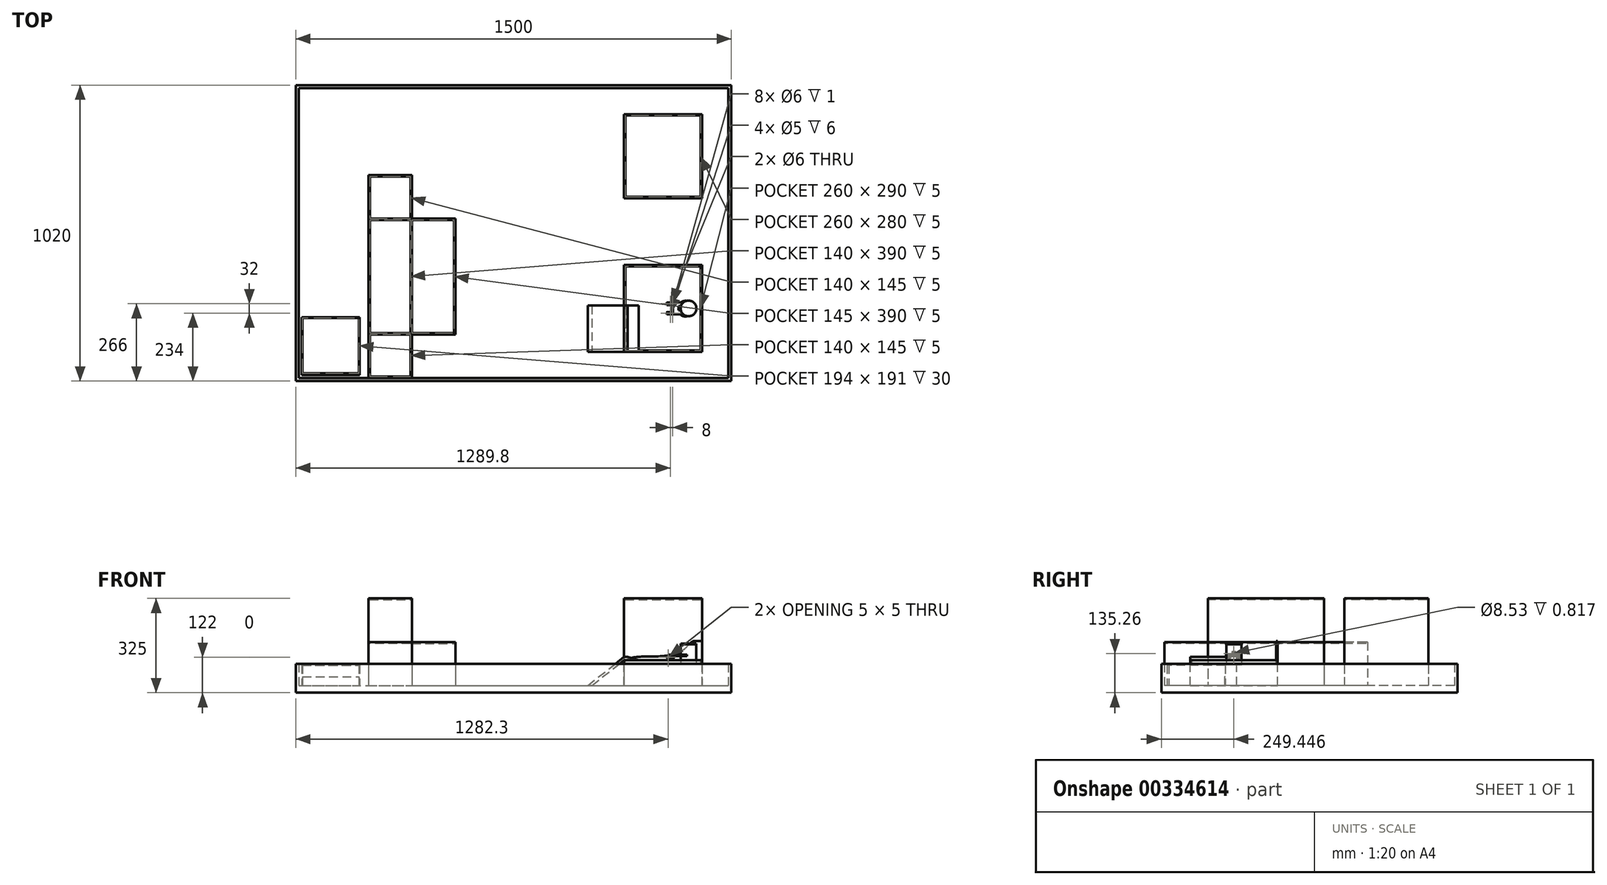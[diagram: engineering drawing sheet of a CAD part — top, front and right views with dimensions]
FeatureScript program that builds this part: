
annotation { "Feature Type Name" : "Feature", "Feature Type Description" : "" }
export const myFeature = defineFeature(function(context is Context, id is Id, definition is map)
    precondition{}
    {
        {
            var Q0;
            Q0=qCreatedBy(makeId("Top.planeOp"),FACE);
            var sketch = newSketch(context, id + "F0", { "sketchPlane" : qUnion([Q0])});
            skCircle(sketch, "E0", {"center": v(0, 0) * mm, "radius": 27.2 * mm});
            skSolve(sketch);
        }
        {
            var Q0;
            Q0=qSketchRegion(id+"F0",true);
            extrude(context, id + "F1", {"entities" : qUnion([Q0]), "depth" : 2.83 * mm});
        }
        {
            var Q0;
            Q0=makeQuery(id+"F1.opExtrude","CAP_FACE",FACE,{"disambiguationData":[OSD([sQuery(id+"F0.wireOp",EDGE,"E0")])],"isStart":false});
            var sketch = newSketch(context, id + "F2", { "sketchPlane" : qUnion([Q0])});
            skCircle(sketch, "E1", {"center": v(0, 0) * mm, "radius": 26.4 * mm});
            skSolve(sketch);
        }
        {
            var Q0;
            Q0=qSketchRegion(id+"F2",true);
            extrude(context, id + "F3", {"entities" : qUnion([Q0]), "operationType" : NewBodyOperationType.ADD, "depth" : 67.36 * mm});
        }
        {
            var Q0;
            Q0=makeQuery(id+"F3.opExtrude","CAP_FACE",FACE,{"disambiguationData":[OSD([sQuery(id+"F2.wireOp",EDGE,"E1")])],"isStart":false});
            var sketch = newSketch(context, id + "F4", { "sketchPlane" : qUnion([Q0])});
            skCircle(sketch, "E2", {"center": v(0, 0) * mm, "radius": 27.2 * mm});
            skSolve(sketch);
        }
        {
            var Q0;
            Q0=qSketchRegion(id+"F4",true);
            extrude(context, id + "F5", {"entities" : qUnion([Q0]), "operationType" : NewBodyOperationType.ADD, "depth" : 2.83 * mm});
        }
        {
            var Q0;
            Q0=makeQuery(id+"F5.opExtrude","CAP_FACE",FACE,{"disambiguationData":[OSD([sQuery(id+"F4.wireOp",EDGE,"E2")])],"isStart":false});
            var sketch = newSketch(context, id + "F6", { "sketchPlane" : qUnion([Q0])});
            skSolve(sketch);
        }
        {
            var Q0;
            Q0=qCreatedBy(makeId("Top.planeOp"),FACE);
            cPlane(context, id + "F7", {"entities" : qUnion([Q0]), "cplaneType" : CPlaneType.OFFSET, "offset" : 25 * mm, "width" : 150 * mm, "height" : 150 * mm});
        }
        {
            var Q0;
            Q0=makeQuery(id+"F6.imprint","IMPRINT",FACE,{"disambiguationData":[TD([[makeQuery(id+"F6.imprint","IMPRINT",EDGE,{"derivedFrom":makeQuery(id+"F5.opExtrude","CAP_EDGE",EDGE,{"disambiguationData":[OSD([sQuery(id+"F4.wireOp",EDGE,"E2")])],"isStart":false})}),1.0]])]});
            var sketch = newSketch(context, id + "F8", { "sketchPlane" : qUnion([Q0])});
            skSolve(sketch);
        }
        {
            var Q0;
            Q0=qCreatedBy(makeId("Top.planeOp"),FACE);
            var sketch = newSketch(context, id + "F9", { "sketchPlane" : qUnion([Q0])});
            skLineSegment(sketch, "E3.bottom", {"start": v(-222.8, -150) * mm, "end": v(47.2, -150) * mm});
            skLineSegment(sketch, "E3.top", {"start": v(-222.8, 150) * mm, "end": v(47.2, 150) * mm});
            skLineSegment(sketch, "E3.left", {"start": v(-222.8, -150) * mm, "end": v(-222.8, 150) * mm});
            skLineSegment(sketch, "E3.right", {"start": v(47.2, -150) * mm, "end": v(47.2, 150) * mm});
            skSolve(sketch);
        }
        {
            var Q0;
            Q0=qSketchRegion(id+"F9",true);
            extrude(context, id + "F10", {"entities" : qUnion([Q0]), "oppositeDirection" : true, "depth" : 72 * mm});
        }
        {
            var Q0;
            Q0=makeQuery(id+"F10.opExtrude","CAP_FACE",FACE,{"disambiguationData":[OSD([sQuery(id+"F9.wireOp",EDGE,"E3.bottom"),sQuery(id+"F9.wireOp",EDGE,"E3.top"),sQuery(id+"F9.wireOp",EDGE,"E3.left"),sQuery(id+"F9.wireOp",EDGE,"E3.right")])],"isStart":true});
            var sketch = newSketch(context, id + "F11", { "sketchPlane" : qUnion([Q0])});
            skLineSegment(sketch, "E4.bottom", {"start": v(-222.8, -150) * mm, "end": v(47.2, -150) * mm});
            skLineSegment(sketch, "E4.top", {"start": v(-222.8, -145) * mm, "end": v(42.2, -145) * mm});
            skLineSegment(sketch, "E4.left", {"start": v(-222.8, -150) * mm, "end": v(-222.8, -145) * mm});
            skLineSegment(sketch, "E5.bottom", {"start": v(47.2, 150) * mm, "end": v(42.2, 150) * mm});
            skLineSegment(sketch, "E5.left", {"start": v(47.2, 150) * mm, "end": v(47.2, -150) * mm});
            skLineSegment(sketch, "E5.right", {"start": v(42.2, 150) * mm, "end": v(42.2, -145) * mm});
            skSolve(sketch);
        }
        {
            var Q0;
            Q0=qSketchRegion(id+"F11",true);
            extrude(context, id + "F12", {"entities" : qUnion([Q0]), "operationType" : NewBodyOperationType.ADD, "depth" : 15 * mm});
        }
        {
            var Q0;
            Q0=makeQuery(id+"F12.boolean.opBoolean","MERGE",FACE,{"derivedFrom":[makeQuery(id+"F10.opExtrude","SWEPT_FACE",FACE,{"disambiguationData":[OSD([sQuery(id+"F9.wireOp",EDGE,"E3.top")])]}),makeQuery(id+"F12.opExtrude","SWEPT_FACE",FACE,{"disambiguationData":[OSD([sQuery(id+"F11.wireOp",EDGE,"E5.bottom")])]})]});
            var sketch = newSketch(context, id + "F13", { "sketchPlane" : qUnion([Q0])});
            skLineSegment(sketch, "E6", {"start": v(-47.2, 81.36) * mm, "end": v(-21.31, 81.36) * mm});
            skFitSpline(sketch, "E7", {"points": [v(-21.31, 81.36) * mm, v(15.24, 52.01) * mm, v(114.14, 28.17) * mm, v(222.8, 0) * mm], "startDerivative": vector(181.02, 0.3) * mm, "endDerivative": vector(-1.73, -239.85) * mm});
            skLineSegment(sketch, "E8", {"start": v(-47.2, 81.36) * mm, "end": v(-47.2, -72) * mm});
            skLineSegment(sketch, "E9", {"start": v(-47.2, -72) * mm, "end": v(222.8, -72) * mm});
            skLineSegment(sketch, "E10", {"start": v(222.8, -72) * mm, "end": v(222.8, 0) * mm});
            skSolve(sketch);
        }
        {
            var Q0;
            Q0=qSketchRegion(id+"F13",true);
            extrude(context, id + "F14", {"entities" : qUnion([Q0]), "operationType" : NewBodyOperationType.ADD, "oppositeDirection" : true, "depth" : 5 * mm});
        }
        {
            var Q0;
            Q0=makeQuery(id+"F10.opExtrude","CAP_FACE",FACE,{"disambiguationData":[OSD([sQuery(id+"F9.wireOp",EDGE,"E3.bottom"),sQuery(id+"F9.wireOp",EDGE,"E3.top"),sQuery(id+"F9.wireOp",EDGE,"E3.left"),sQuery(id+"F9.wireOp",EDGE,"E3.right")])],"isStart":true});
            var sketch = newSketch(context, id + "F15", { "sketchPlane" : qUnion([Q0])});
            skLineSegment(sketch, "E11.bottom", {"start": v(-222.8, 145) * mm, "end": v(-217.8, 145) * mm});
            skLineSegment(sketch, "E11.top", {"start": v(-222.8, -145) * mm, "end": v(-217.8, -145) * mm});
            skLineSegment(sketch, "E11.left", {"start": v(-222.8, 145) * mm, "end": v(-222.8, -145) * mm});
            skLineSegment(sketch, "E11.right", {"start": v(-217.8, 145) * mm, "end": v(-217.8, -145) * mm});
            skSolve(sketch);
        }
        {
            var Q0;
            Q0=qSketchRegion(id+"F15",true);
            extrude(context, id + "F16", {"entities" : qUnion([Q0]), "operationType" : NewBodyOperationType.ADD, "depth" : 5 * mm});
        }
        {
            var Q0;
            Q0=makeQuery(id+"F10.opExtrude","CAP_FACE",FACE,{"disambiguationData":[OSD([sQuery(id+"F9.wireOp",EDGE,"E3.bottom"),sQuery(id+"F9.wireOp",EDGE,"E3.top"),sQuery(id+"F9.wireOp",EDGE,"E3.left"),sQuery(id+"F9.wireOp",EDGE,"E3.right")])],"isStart":false});
            var sketch = newSketch(context, id + "F17", { "sketchPlane" : qUnion([Q0])});
            skLineSegment(sketch, "E12.bottom", {"start": v(147.2, 250) * mm, "end": v(-1352.8, 250) * mm});
            skLineSegment(sketch, "E12.top", {"start": v(147.2, -770) * mm, "end": v(-1352.8, -770) * mm});
            skLineSegment(sketch, "E12.left", {"start": v(147.2, 250) * mm, "end": v(147.2, -770) * mm});
            skLineSegment(sketch, "E12.right", {"start": v(-1352.8, 250) * mm, "end": v(-1352.8, -770) * mm});
            skSolve(sketch);
        }
        {
            var Q0;
            Q0=qSketchRegion(id+"F17",true);
            extrude(context, id + "F18", {"entities" : qUnion([Q0]), "operationType" : NewBodyOperationType.ADD, "depth" : 25 * mm});
        }
        {
            var Q0;
            Q0=makeQuery(id+"F18.opExtrude","CAP_FACE",FACE,{"disambiguationData":[OSD([sQuery(id+"F17.wireOp",EDGE,"E12.bottom"),sQuery(id+"F17.wireOp",EDGE,"E12.top"),sQuery(id+"F17.wireOp",EDGE,"E12.left"),sQuery(id+"F17.wireOp",EDGE,"E12.right")])],"isStart":true});
            var sketch = newSketch(context, id + "F19", { "sketchPlane" : qUnion([Q0])});
            skLineSegment(sketch, "E13.bottom", {"start": v(-222.8, 670) * mm, "end": v(47.2, 670) * mm});
            skLineSegment(sketch, "E13.top", {"start": v(-222.8, 380) * mm, "end": v(47.2, 380) * mm});
            skLineSegment(sketch, "E13.left", {"start": v(-222.8, 670) * mm, "end": v(-222.8, 380) * mm});
            skLineSegment(sketch, "E13.right", {"start": v(47.2, 670) * mm, "end": v(47.2, 380) * mm});
            skSolve(sketch);
        }
        {
            var Q0;
            Q0=qSketchRegion(id+"F19",true);
            extrude(context, id + "F20", {"entities" : qUnion([Q0]), "operationType" : NewBodyOperationType.ADD, "depth" : 300 * mm});
        }
        {
            var Q0;
            Q0=makeQuery(id+"F20.opExtrude","CAP_FACE",FACE,{"disambiguationData":[OSD([sQuery(id+"F19.wireOp",EDGE,"E13.bottom"),sQuery(id+"F19.wireOp",EDGE,"E13.top"),sQuery(id+"F19.wireOp",EDGE,"E13.left"),sQuery(id+"F19.wireOp",EDGE,"E13.right")])],"isStart":false});
            var sketch = newSketch(context, id + "F21", { "sketchPlane" : qUnion([Q0])});
            skLineSegment(sketch, "E14.bottom", {"start": v(-217.8, 665) * mm, "end": v(42.2, 665) * mm});
            skLineSegment(sketch, "E14.top", {"start": v(-217.8, 385) * mm, "end": v(42.2, 385) * mm});
            skLineSegment(sketch, "E14.left", {"start": v(-217.8, 665) * mm, "end": v(-217.8, 385) * mm});
            skLineSegment(sketch, "E14.right", {"start": v(42.2, 665) * mm, "end": v(42.2, 385) * mm});
            skSolve(sketch);
        }
        {
            var Q0;
            Q0=qSketchRegion(id+"F21",true);
            extrude(context, id + "F22", {"entities" : qUnion([Q0]), "operationType" : NewBodyOperationType.REMOVE, "oppositeDirection" : true, "depth" : 5 * mm});
        }
        {
            var Q0;
            Q0=makeQuery(id+"F18.opExtrude","CAP_FACE",FACE,{"disambiguationData":[OSD([sQuery(id+"F17.wireOp",EDGE,"E12.bottom"),sQuery(id+"F17.wireOp",EDGE,"E12.top"),sQuery(id+"F17.wireOp",EDGE,"E12.left"),sQuery(id+"F17.wireOp",EDGE,"E12.right")])],"isStart":true});
            var sketch = newSketch(context, id + "F23", { "sketchPlane" : qUnion([Q0])});
            skLineSegment(sketch, "E15.bottom", {"start": v(-1352.8, 770) * mm, "end": v(147.2, 770) * mm});
            skLineSegment(sketch, "E15.top", {"start": v(-1352.8, -250) * mm, "end": v(147.2, -250) * mm});
            skLineSegment(sketch, "E15.left", {"start": v(-1352.8, 770) * mm, "end": v(-1352.8, -250) * mm});
            skLineSegment(sketch, "E15.right", {"start": v(147.2, 770) * mm, "end": v(147.2, -250) * mm});
            skLineSegment(sketch, "E16.bottom", {"start": v(-1342.8, 760) * mm, "end": v(137.2, 760) * mm});
            skLineSegment(sketch, "E16.top", {"start": v(-1342.8, -240) * mm, "end": v(137.2, -240) * mm});
            skLineSegment(sketch, "E16.left", {"start": v(-1342.8, 760) * mm, "end": v(-1342.8, -240) * mm});
            skLineSegment(sketch, "E16.right", {"start": v(137.2, 760) * mm, "end": v(137.2, -240) * mm});
            skSolve(sketch);
        }
        {
            var Q0;
            Q0=qSketchRegion(id+"F23",true);
            extrude(context, id + "F24", {"entities" : qUnion([Q0]), "operationType" : NewBodyOperationType.ADD, "depth" : 75 * mm});
        }
        {
            var Q0;
            Q0=makeQuery(id+"F18.opExtrude","CAP_FACE",FACE,{"disambiguationData":[OSD([sQuery(id+"F17.wireOp",EDGE,"E12.bottom"),sQuery(id+"F17.wireOp",EDGE,"E12.top"),sQuery(id+"F17.wireOp",EDGE,"E12.left"),sQuery(id+"F17.wireOp",EDGE,"E12.right")])],"isStart":true});
            var sketch = newSketch(context, id + "F25", { "sketchPlane" : qUnion([Q0])});
            skLineSegment(sketch, "E17.bottom", {"start": v(-1102.8, 460) * mm, "end": v(-952.8, 460) * mm});
            skLineSegment(sketch, "E17.top", {"start": v(-1102.8, -240) * mm, "end": v(-952.8, -240) * mm});
            skLineSegment(sketch, "E17.left", {"start": v(-1102.8, 460) * mm, "end": v(-1102.8, -240) * mm});
            skLineSegment(sketch, "E17.right", {"start": v(-952.8, 460) * mm, "end": v(-952.8, 310) * mm});
            skLineSegment(sketch, "E18.bottom", {"start": v(-952.8, 310) * mm, "end": v(-802.8, 310) * mm});
            skLineSegment(sketch, "E18.top", {"start": v(-952.8, -90) * mm, "end": v(-802.8, -90) * mm});
            skLineSegment(sketch, "E18.right", {"start": v(-802.8, 310) * mm, "end": v(-802.8, -90) * mm});
            skLineSegment(sketch, "E19.trimOffspring", {"start": v(-952.8, -90) * mm, "end": v(-952.8, -240) * mm});
            skSolve(sketch);
        }
        {
            var Q0;
            Q0=qSketchRegion(id+"F25",true);
            extrude(context, id + "F26", {"entities" : qUnion([Q0]), "operationType" : NewBodyOperationType.ADD, "depth" : 150 * mm});
        }
        {
            var Q0;
            Q0=makeQuery(id+"F26.opExtrude","CAP_FACE",FACE,{"disambiguationData":[OSD([sQuery(id+"F25.wireOp",EDGE,"E17.bottom"),sQuery(id+"F25.wireOp",EDGE,"E17.top"),sQuery(id+"F25.wireOp",EDGE,"E17.left"),sQuery(id+"F25.wireOp",EDGE,"E17.right"),sQuery(id+"F25.wireOp",EDGE,"E18.bottom"),sQuery(id+"F25.wireOp",EDGE,"E18.top"),sQuery(id+"F25.wireOp",EDGE,"E18.right"),sQuery(id+"F25.wireOp",EDGE,"E19.trimOffspring")])],"isStart":false});
            var sketch = newSketch(context, id + "F27", { "sketchPlane" : qUnion([Q0])});
            skLineSegment(sketch, "E20.bottom", {"start": v(-952.8, 310) * mm, "end": v(-1102.8, 310) * mm});
            skLineSegment(sketch, "E20.top", {"start": v(-952.8, -90) * mm, "end": v(-1102.8, -90) * mm});
            skLineSegment(sketch, "E20.left", {"start": v(-952.8, 310) * mm, "end": v(-952.8, -90) * mm});
            skLineSegment(sketch, "E20.right", {"start": v(-1102.8, 310) * mm, "end": v(-1102.8, -90) * mm});
            skSolve(sketch);
        }
        {
            var Q0;
            Q0=qSketchRegion(id+"F27",true);
            extrude(context, id + "F28", {"entities" : qUnion([Q0]), "operationType" : NewBodyOperationType.ADD, "depth" : 150 * mm});
        }
        {
            var Q0;
            Q0=makeQuery(id+"F28.opExtrude","CAP_FACE",FACE,{"disambiguationData":[OSD([sQuery(id+"F27.wireOp",EDGE,"E20.bottom"),sQuery(id+"F27.wireOp",EDGE,"E20.top"),sQuery(id+"F27.wireOp",EDGE,"E20.left"),sQuery(id+"F27.wireOp",EDGE,"E20.right")])],"isStart":false});
            var sketch = newSketch(context, id + "F29", { "sketchPlane" : qUnion([Q0])});
            skLineSegment(sketch, "E21.bottom", {"start": v(-1097.8, 305) * mm, "end": v(-957.8, 305) * mm});
            skLineSegment(sketch, "E21.top", {"start": v(-1097.8, -85) * mm, "end": v(-957.8, -85) * mm});
            skLineSegment(sketch, "E21.left", {"start": v(-1097.8, 305) * mm, "end": v(-1097.8, -85) * mm});
            skLineSegment(sketch, "E21.right", {"start": v(-957.8, 305) * mm, "end": v(-957.8, -85) * mm});
            skSolve(sketch);
        }
        {
            var Q0;
            Q0=qSketchRegion(id+"F29",true);
            extrude(context, id + "F30", {"entities" : qUnion([Q0]), "operationType" : NewBodyOperationType.REMOVE, "oppositeDirection" : true, "depth" : 5 * mm});
        }
        {
            var Q0;
            {var subQ0=sQuery(id+"F25.wireOp",EDGE,"E17.left");var subQ1=sQuery(id+"F25.wireOp",EDGE,"E18.bottom");var subQ2=sQuery(id+"F25.wireOp",EDGE,"E17.right");var subQ3=sQuery(id+"F25.wireOp",EDGE,"E17.bottom");var subQ4=makeQuery(id+"F26.opExtrude","CAP_FACE",FACE,{"disambiguationData":[OSD([subQ3,sQuery(id+"F25.wireOp",EDGE,"E17.top"),subQ0,subQ2,subQ1,sQuery(id+"F25.wireOp",EDGE,"E18.top"),sQuery(id+"F25.wireOp",EDGE,"E18.right"),sQuery(id+"F25.wireOp",EDGE,"E19.trimOffspring")])],"isStart":false});Q0=makeQuery(id+"F28.boolean.opBoolean","SPLIT",FACE,{"disambiguationData":[TD([makeQuery(id+"F26.opExtrude","SWEPT_FACE",FACE,{"disambiguationData":[OSD([subQ3])]})])],"derivedFrom":subQ4});}
            var sketch = newSketch(context, id + "F31", { "sketchPlane" : qUnion([Q0])});
            skLineSegment(sketch, "E22.bottom", {"start": v(-1097.8, 455) * mm, "end": v(-957.8, 455) * mm});
            skLineSegment(sketch, "E22.top", {"start": v(-1097.8, 310) * mm, "end": v(-957.8, 310) * mm});
            skLineSegment(sketch, "E22.left", {"start": v(-1097.8, 455) * mm, "end": v(-1097.8, 310) * mm});
            skLineSegment(sketch, "E22.right", {"start": v(-957.8, 455) * mm, "end": v(-957.8, 310) * mm});
            skLineSegment(sketch, "E23.bottom", {"start": v(-952.8, 305) * mm, "end": v(-807.8, 305) * mm});
            skLineSegment(sketch, "E23.top", {"start": v(-952.8, -85) * mm, "end": v(-807.8, -85) * mm});
            skLineSegment(sketch, "E23.left", {"start": v(-952.8, 305) * mm, "end": v(-952.8, -85) * mm});
            skLineSegment(sketch, "E23.right", {"start": v(-807.8, 305) * mm, "end": v(-807.8, -85) * mm});
            skLineSegment(sketch, "E24.bottom", {"start": v(-1097.8, -90) * mm, "end": v(-957.8, -90) * mm});
            skLineSegment(sketch, "E24.top", {"start": v(-1097.8, -235) * mm, "end": v(-957.8, -235) * mm});
            skLineSegment(sketch, "E24.left", {"start": v(-1097.8, -90) * mm, "end": v(-1097.8, -235) * mm});
            skLineSegment(sketch, "E24.right", {"start": v(-957.8, -90) * mm, "end": v(-957.8, -235) * mm});
            skSolve(sketch);
        }
        {
            var Q0;
            Q0=qSketchRegion(id+"F31",true);
            extrude(context, id + "F32", {"entities" : qUnion([Q0]), "operationType" : NewBodyOperationType.REMOVE, "oppositeDirection" : true, "depth" : 5 * mm});
        }
        {
            var Q0;
            Q0=qCreatedBy(id+"F7.planeOp",FACE);
            var sketch = newSketch(context, id + "F33", { "sketchPlane" : qUnion([Q0])});
            skLineSegment(sketch, "E25", {"start": v(0, 0) * mm, "end": v(-90, 0) * mm, "construction": true});
            skLineSegment(sketch, "E26.bottom", {"start": v(-74.5, -12) * mm, "end": v(-55, -12) * mm});
            skLineSegment(sketch, "E26.top", {"start": v(-74.5, -20) * mm, "end": v(-55, -20) * mm});
            skLineSegment(sketch, "E26.left", {"start": v(-74.5, -12) * mm, "end": v(-74.5, -13) * mm});
            skPoint(sketch, "E27.visualSharp", {"position": v(-51, -12) * mm});
            skPoint(sketch, "E28.visualSharp", {"position": v(-51, -20) * mm});
            skCircle(sketch, "E29", {"center": v(-55, -16) * mm, "radius": 3 * mm});
            skLineSegment(sketch, "E30", {"start": v(-59, -3.98) * mm, "end": v(-59, -18.08) * mm, "construction": true});
            skCircle(sketch, "E31.MirrorC", {"center": v(-63, -16) * mm, "radius": 3 * mm});
            skLineSegment(sketch, "E32.bottom", {"start": v(-74.5, -13) * mm, "end": v(-65.65, -13) * mm});
            skLineSegment(sketch, "E32.top", {"start": v(-74.5, -19) * mm, "end": v(-65.65, -19) * mm});
            skArc(sketch, "E33", {"start": v(-65.65, -13) * mm, "mid": v(-67, -16) * mm, "end": v(-65.65, -19) * mm});
            skLineSegment(sketch, "E34.trimOffspring", {"start": v(-74.5, -19) * mm, "end": v(-74.5, -20) * mm});
            skArc(sketch, "E35.trimOffspring", {"start": v(-55, -20) * mm, "mid": v(-51, -16) * mm, "end": v(-55, -12) * mm});
            skLineSegment(sketch, "E36.MirrorCS", {"start": v(-74.5, 12) * mm, "end": v(-74.5, 13) * mm});
            skLineSegment(sketch, "E37.MirrorCS", {"start": v(-74.5, 19) * mm, "end": v(-74.5, 20) * mm});
            skPoint(sketch, "E38.MirrorP", {"position": v(-51, 12) * mm});
            skLineSegment(sketch, "E39.MirrorCS", {"start": v(-74.5, 12) * mm, "end": v(-55, 12) * mm});
            skPoint(sketch, "E40.MirrorP", {"position": v(-51, 20) * mm});
            skArc(sketch, "E41.MirrorCS", {"start": v(-65.65, 13) * mm, "mid": v(-67, 16) * mm, "end": v(-65.65, 19) * mm});
            skArc(sketch, "E42.MirrorCS", {"start": v(-55, 20) * mm, "mid": v(-51, 16) * mm, "end": v(-55, 12) * mm});
            skLineSegment(sketch, "E43.MirrorCS", {"start": v(-74.5, 20) * mm, "end": v(-55, 20) * mm});
            skCircle(sketch, "E44.MirrorC", {"center": v(-55, 16) * mm, "radius": 3 * mm});
            skCircle(sketch, "E45.MirrorC", {"center": v(-63, 16) * mm, "radius": 3 * mm});
            skLineSegment(sketch, "E46.MirrorCS", {"start": v(-74.5, 19) * mm, "end": v(-65.65, 19) * mm});
            skLineSegment(sketch, "E47.MirrorCS", {"start": v(-74.5, 13) * mm, "end": v(-65.65, 13) * mm});
            skSolve(sketch);
        }
        {
            var Q0;
            Q0=qSketchRegion(id+"F33",true);
            var Q1;
            Q1=qSketchRegion(id+"F36",true);
            extrude(context, id + "F34", {"entities" : qUnion([Q0, Q1]), "endBound" : BoundingType.SYMMETRIC, "depth" : 8 * mm});
        }
        {
            var Q0;
            Q0=makeQuery(id+"F34.opExtrude","CAP_EDGE",EDGE,{"disambiguationData":[OSD([sQuery(id+"F33.wireOp",EDGE,"E34.trimOffspring")])],"isStart":false});
            var Q1;
            Q1=makeQuery(id+"F34.opExtrude","CAP_EDGE",EDGE,{"disambiguationData":[OSD([sQuery(id+"F33.wireOp",EDGE,"E26.left")])],"isStart":false});
            var Q2;
            Q2=makeQuery(id+"F34.opExtrude","CAP_EDGE",EDGE,{"disambiguationData":[OSD([sQuery(id+"F33.wireOp",EDGE,"E34.trimOffspring")])],"isStart":true});
            var Q3;
            Q3=makeQuery(id+"F34.opExtrude","CAP_EDGE",EDGE,{"disambiguationData":[OSD([sQuery(id+"F33.wireOp",EDGE,"E26.left")])],"isStart":true});
            var Q4;
            Q4=makeQuery(id+"F34.opExtrude","CAP_EDGE",EDGE,{"disambiguationData":[OSD([sQuery(id+"F33.wireOp",EDGE,"E36.MirrorCS")])],"isStart":false});
            var Q5;
            Q5=makeQuery(id+"F34.opExtrude","CAP_EDGE",EDGE,{"disambiguationData":[OSD([sQuery(id+"F33.wireOp",EDGE,"E37.MirrorCS")])],"isStart":false});
            var Q6;
            Q6=makeQuery(id+"F34.opExtrude","CAP_EDGE",EDGE,{"disambiguationData":[OSD([sQuery(id+"F33.wireOp",EDGE,"E37.MirrorCS")])],"isStart":true});
            var Q7;
            Q7=makeQuery(id+"F34.opExtrude","CAP_EDGE",EDGE,{"disambiguationData":[OSD([sQuery(id+"F33.wireOp",EDGE,"E36.MirrorCS")])],"isStart":true});
            fillet(context, id + "F35", {"entities" : qUnion([Q0, Q1, Q2, Q3, Q4, Q5, Q6, Q7]), "radius" : 4 * mm, "tangentPropagation" : true, "allowEdgeOverflow" : false});
        }
        {
            var Q0;
            Q0=makeQuery(id+"F34.opExtrude","SWEPT_FACE",FACE,{"disambiguationData":[OSD([sQuery(id+"F33.wireOp",EDGE,"E26.top")])]});
            var sketch = newSketch(context, id + "F36", { "sketchPlane" : qUnion([Q0])});
            skCircle(sketch, "E48", {"center": v(-70.5, 25) * mm, "radius": 3 * mm});
            skSolve(sketch);
        }
        {
            var Q0;
            Q0=qSketchRegion(id+"F36",true);
            var Q1;
            Q1=makeQuery(id+"F34.opExtrude","SWEPT_FACE",FACE,{"disambiguationData":[OSD([sQuery(id+"F33.wireOp",EDGE,"E26.bottom")])]});
            extrude(context, id + "F37", {"entities" : qUnion([Q0]), "operationType" : NewBodyOperationType.ADD, "endBound" : BoundingType.UP_TO_SURFACE, "oppositeDirection" : true, "endBoundEntityFace" : qUnion([Q1]), "depth" : 25 * mm});
        }
        {
            var Q0;
            Q0=makeQuery(id+"F34.opExtrude","SWEPT_FACE",FACE,{"disambiguationData":[OSD([sQuery(id+"F33.wireOp",EDGE,"E43.MirrorCS")])]});
            var sketch = newSketch(context, id + "F38", { "sketchPlane" : qUnion([Q0])});
            skCircle(sketch, "E49", {"center": v(70.5, 25) * mm, "radius": 3 * mm});
            skSolve(sketch);
        }
        {
            var Q0;
            Q0=qSketchRegion(id+"F38",true);
            var Q1;
            Q1=makeQuery(id+"F34.opExtrude","SWEPT_FACE",FACE,{"disambiguationData":[OSD([sQuery(id+"F33.wireOp",EDGE,"E39.MirrorCS")])]});
            extrude(context, id + "F39", {"entities" : qUnion([Q0]), "operationType" : NewBodyOperationType.ADD, "endBound" : BoundingType.UP_TO_SURFACE, "oppositeDirection" : true, "endBoundEntityFace" : qUnion([Q1]), "depth" : 25 * mm});
        }
        {
            var Q0;
            Q0=qCreatedBy(id+"F7.planeOp",FACE);
            var sketch = newSketch(context, id + "F40", { "sketchPlane" : qUnion([Q0])});
            skCircle(sketch, "E50", {"center": v(-55, 16) * mm, "radius": 3 * mm});
            skCircle(sketch, "E51", {"center": v(-63, 16) * mm, "radius": 2.5 * mm});
            skCircle(sketch, "E52", {"center": v(-63, 16) * mm, "radius": 3 * mm});
            skCircle(sketch, "E53", {"center": v(-55, 16) * mm, "radius": 2.5 * mm});
            skSolve(sketch);
        }
        {
            var Q0;
            Q0=qSketchRegion(id+"F40",true);
            extrude(context, id + "F41", {"entities" : qUnion([Q0]), "operationType" : NewBodyOperationType.ADD, "endBound" : BoundingType.SYMMETRIC, "depth" : 6 * mm});
        }
        {
            var Q0;
            Q0=qCreatedBy(id+"F7.planeOp",FACE);
            var sketch = newSketch(context, id + "F42", { "sketchPlane" : qUnion([Q0])});
            skCircle(sketch, "E54", {"center": v(-63, -16) * mm, "radius": 2.5 * mm});
            skCircle(sketch, "E55", {"center": v(-63, -16) * mm, "radius": 3 * mm});
            skCircle(sketch, "E56", {"center": v(-55, -16) * mm, "radius": 2.5 * mm});
            skCircle(sketch, "E57", {"center": v(-55, -16) * mm, "radius": 3 * mm});
            skSolve(sketch);
        }
        {
            var Q0;
            Q0=qSketchRegion(id+"F42",true);
            extrude(context, id + "F43", {"entities" : qUnion([Q0]), "operationType" : NewBodyOperationType.ADD, "endBound" : BoundingType.SYMMETRIC, "depth" : 6 * mm});
        }
        {
            var Q0;
            Q0=makeQuery(id+"F34.opExtrude","SWEPT_FACE",FACE,{"disambiguationData":[OSD([sQuery(id+"F33.wireOp",EDGE,"E43.MirrorCS")])]});
            var sketch = newSketch(context, id + "F44", { "sketchPlane" : qUnion([Q0])});
            skArc(sketch, "E58", {"start": v(71.5, 27.3) * mm, "mid": v(70.5, 27.5) * mm, "end": v(69.5, 27.3) * mm});
            skLineSegment(sketch, "E59.bottom", {"start": v(68.2, 26) * mm, "end": v(69.5, 26) * mm});
            skLineSegment(sketch, "E59.top", {"start": v(68.2, 24) * mm, "end": v(69.5, 24) * mm});
            skLineSegment(sketch, "E60.left", {"start": v(71.5, 27.3) * mm, "end": v(71.5, 26) * mm});
            skLineSegment(sketch, "E60.right", {"start": v(69.5, 27.3) * mm, "end": v(69.5, 26) * mm});
            skPoint(sketch, "E61.orphan", {"position": v(69.5, 27.8) * mm});
            skPoint(sketch, "E62.orphan", {"position": v(71.5, 27.8) * mm});
            skArc(sketch, "E63.trimOffspring", {"start": v(68.2, 26) * mm, "mid": v(68, 25) * mm, "end": v(68.2, 24) * mm});
            skPoint(sketch, "E59.left.start.orphan", {"position": v(67.32, 26) * mm});
            skPoint(sketch, "E64.orphan", {"position": v(67.32, 24) * mm});
            skArc(sketch, "E65.trimOffspring", {"start": v(69.5, 22.7) * mm, "mid": v(70.5, 22.5) * mm, "end": v(71.5, 22.7) * mm});
            skLineSegment(sketch, "E66.trimOffspring", {"start": v(69.5, 24) * mm, "end": v(69.5, 22.7) * mm});
            skLineSegment(sketch, "E67.trimOffspring", {"start": v(71.5, 26) * mm, "end": v(72.8, 26) * mm});
            skLineSegment(sketch, "E68.trimOffspring", {"start": v(71.5, 24) * mm, "end": v(71.5, 22.7) * mm});
            skLineSegment(sketch, "E69.trimOffspring", {"start": v(71.5, 24) * mm, "end": v(72.8, 24) * mm});
            skPoint(sketch, "E60.top.end.orphan", {"position": v(69.5, 22.2) * mm});
            skPoint(sketch, "E70.orphan", {"position": v(71.5, 22.2) * mm});
            skPoint(sketch, "E59.right.end.orphan", {"position": v(73.68, 24) * mm});
            skPoint(sketch, "E71.orphan", {"position": v(73.68, 26) * mm});
            skArc(sketch, "E72.trimOffspring", {"start": v(72.8, 24) * mm, "mid": v(73, 25) * mm, "end": v(72.8, 26) * mm});
            skSolve(sketch);
        }
        {
            var Q0;
            Q0=qSketchRegion(id+"F44",true);
            extrude(context, id + "F45", {"entities" : qUnion([Q0]), "operationType" : NewBodyOperationType.REMOVE, "endBound" : BoundingType.THROUGH_ALL, "oppositeDirection" : true, "depth" : 25 * mm});
        }
        {
            var Q0;
            Q0=makeQuery(id+"F18.opExtrude","CAP_FACE",FACE,{"disambiguationData":[OSD([sQuery(id+"F17.wireOp",EDGE,"E12.bottom"),sQuery(id+"F17.wireOp",EDGE,"E12.top"),sQuery(id+"F17.wireOp",EDGE,"E12.left"),sQuery(id+"F17.wireOp",EDGE,"E12.right")])],"isStart":true});
            var sketch = newSketch(context, id + "F46", { "sketchPlane" : qUnion([Q0])});
            skLineSegment(sketch, "E73.bottom", {"start": v(-1332.8, -30) * mm, "end": v(-1132.8, -30) * mm});
            skLineSegment(sketch, "E73.top", {"start": v(-1332.8, -230) * mm, "end": v(-1132.8, -230) * mm});
            skLineSegment(sketch, "E73.left", {"start": v(-1332.8, -30) * mm, "end": v(-1332.8, -230) * mm});
            skLineSegment(sketch, "E73.right", {"start": v(-1132.8, -30) * mm, "end": v(-1132.8, -230) * mm});
            skLineSegment(sketch, "E74.bottom", {"start": v(-1329.8, -33) * mm, "end": v(-1135.8, -33) * mm});
            skLineSegment(sketch, "E74.top", {"start": v(-1329.8, -224) * mm, "end": v(-1135.8, -224) * mm});
            skLineSegment(sketch, "E74.left", {"start": v(-1329.8, -33) * mm, "end": v(-1329.8, -224) * mm});
            skLineSegment(sketch, "E74.right", {"start": v(-1135.8, -33) * mm, "end": v(-1135.8, -224) * mm});
            skSolve(sketch);
        }
        {
            var Q0;
            Q0=qSketchRegion(id+"F46",true);
            extrude(context, id + "F47", {"entities" : qUnion([Q0]), "operationType" : NewBodyOperationType.ADD, "depth" : 30 * mm});
        }
        {
            var Q0;
            Q0=makeQuery(id+"F47.opExtrude","CAP_FACE",FACE,{"disambiguationData":[OSD([sQuery(id+"F46.wireOp",EDGE,"E73.bottom"),sQuery(id+"F46.wireOp",EDGE,"E73.top"),sQuery(id+"F46.wireOp",EDGE,"E73.left"),sQuery(id+"F46.wireOp",EDGE,"E73.right"),sQuery(id+"F46.wireOp",EDGE,"E74.bottom"),sQuery(id+"F46.wireOp",EDGE,"E74.top"),sQuery(id+"F46.wireOp",EDGE,"E74.left"),sQuery(id+"F46.wireOp",EDGE,"E74.right")])],"isStart":false});
            var sketch = newSketch(context, id + "F48", { "sketchPlane" : qUnion([Q0])});
            skLineSegment(sketch, "E75.bottom", {"start": v(-1332.8, -30) * mm, "end": v(-1329.8, -30) * mm});
            skLineSegment(sketch, "E75.top", {"start": v(-1332.8, -230) * mm, "end": v(-1329.8, -230) * mm});
            skLineSegment(sketch, "E75.left", {"start": v(-1332.8, -30) * mm, "end": v(-1332.8, -230) * mm});
            skLineSegment(sketch, "E75.right", {"start": v(-1329.8, -30) * mm, "end": v(-1329.8, -224) * mm});
            skLineSegment(sketch, "E76.bottom", {"start": v(-1329.8, -230) * mm, "end": v(-1135.8, -230) * mm});
            skLineSegment(sketch, "E76.top", {"start": v(-1329.8, -224) * mm, "end": v(-1135.8, -224) * mm});
            skLineSegment(sketch, "E77.bottom", {"start": v(-1135.8, -230) * mm, "end": v(-1132.8, -230) * mm});
            skLineSegment(sketch, "E77.top", {"start": v(-1135.8, -30) * mm, "end": v(-1132.8, -30) * mm});
            skLineSegment(sketch, "E77.left", {"start": v(-1135.8, -224) * mm, "end": v(-1135.8, -30) * mm});
            skLineSegment(sketch, "E77.right", {"start": v(-1132.8, -230) * mm, "end": v(-1132.8, -30) * mm});
            skSolve(sketch);
        }
        {
            var Q0;
            Q0=qSketchRegion(id+"F48",true);
            extrude(context, id + "F49", {"entities" : qUnion([Q0]), "operationType" : NewBodyOperationType.ADD, "depth" : 40 * mm});
        }
        {
            var Q0;
            Q0=makeQuery(id+"F34.opExtrude","CAP_FACE",FACE,{"disambiguationData":[OSD([sQuery(id+"F33.wireOp",EDGE,"E36.MirrorCS"),sQuery(id+"F33.wireOp",EDGE,"E37.MirrorCS"),sQuery(id+"F33.wireOp",EDGE,"E39.MirrorCS"),sQuery(id+"F33.wireOp",EDGE,"E41.MirrorCS"),sQuery(id+"F33.wireOp",EDGE,"E42.MirrorCS"),sQuery(id+"F33.wireOp",EDGE,"E43.MirrorCS"),sQuery(id+"F33.wireOp",EDGE,"E44.MirrorC"),sQuery(id+"F33.wireOp",EDGE,"E45.MirrorC"),sQuery(id+"F33.wireOp",EDGE,"E46.MirrorCS"),sQuery(id+"F33.wireOp",EDGE,"E47.MirrorCS")])],"isStart":false});
            var sketch = newSketch(context, id + "F50", { "sketchPlane" : qUnion([Q0])});
            skLineSegment(sketch, "E78.top", {"start": v(-71.23, -20) * mm, "end": v(-29.67, -20) * mm});
            skLineSegment(sketch, "E79.top", {"start": v(-71.23, -12) * mm, "end": v(-53.43, -12) * mm});
            skLineSegment(sketch, "E79.right", {"start": v(-53.43, 12) * mm, "end": v(-53.43, -12) * mm});
            skLineSegment(sketch, "E80.trimOffspring", {"start": v(-71.23, -12) * mm, "end": v(-71.23, -20) * mm});
            skArc(sketch, "E81", {"start": v(-9.36, 26.26) * mm, "mid": v(-27.5, -1.9) * mm, "end": v(-5.25, -26.94) * mm});
            skPoint(sketch, "E81.first.point", {"position": v(-27.57, -0.17) * mm});
            skPoint(sketch, "E81.second.point", {"position": v(-10.03, 26) * mm});
            skPoint(sketch, "E81.third.point", {"position": v(1.83, -27.41) * mm});
            skArc(sketch, "E82", {"start": v(-9.36, 26.26) * mm, "mid": v(-19.42, 24.94) * mm, "end": v(-28.29, 20) * mm});
            skPoint(sketch, "E82.first.point", {"position": v(-28.29, 20) * mm});
            skPoint(sketch, "E82.second.point", {"position": v(-29.67, -20) * mm});
            skPoint(sketch, "E82.third.point", {"position": v(15.79, 2.36) * mm});
            skArc(sketch, "E83.trimOffspring", {"start": v(-29.67, -20) * mm, "mid": v(-18.33, -26.53) * mm, "end": v(-5.25, -26.94) * mm});
            skCircle(sketch, "E84", {"center": v(-55, 16) * mm, "radius": 3 * mm});
            skPoint(sketch, "E84.first.point", {"position": v(-52.66, 14.13) * mm});
            skPoint(sketch, "E84.second.point", {"position": v(-57.5, 17.66) * mm});
            skPoint(sketch, "E84.third.point", {"position": v(-57.2, 13.96) * mm});
            skCircle(sketch, "E85", {"center": v(-63, 16) * mm, "radius": 3 * mm});
            skPoint(sketch, "E85.first.point", {"position": v(-61.25, 13.56) * mm});
            skPoint(sketch, "E85.second.point", {"position": v(-65.2, 18.04) * mm});
            skPoint(sketch, "E85.third.point", {"position": v(-65.14, 13.9) * mm});
            skCircle(sketch, "E86", {"center": v(-55.1, -16) * mm, "radius": 2.29 * mm});
            skPoint(sketch, "E86.first.point", {"position": v(-57.4, -16.07) * mm});
            skPoint(sketch, "E86.second.point", {"position": v(-52.82, -15.93) * mm});
            skPoint(sketch, "E86.third.point", {"position": v(-55, -18.29) * mm});
            skCircle(sketch, "E87", {"center": v(-63.04, -15.8) * mm, "radius": 2.5 * mm});
            skPoint(sketch, "E87.first.point", {"position": v(-63, -18.29) * mm});
            skPoint(sketch, "E87.second.point", {"position": v(-63, -13.3) * mm});
            skPoint(sketch, "E87.third.point", {"position": v(-60.58, -16.2) * mm});
            skLineSegment(sketch, "E88.bottom", {"start": v(-28.29, 20) * mm, "end": v(-71.19, 20) * mm});
            skLineSegment(sketch, "E88.top", {"start": v(-53.43, 12) * mm, "end": v(-71.19, 12) * mm});
            skLineSegment(sketch, "E88.right", {"start": v(-71.19, 20) * mm, "end": v(-71.19, 12) * mm});
            skSolve(sketch);
        }
        {
            var Q0;
            Q0 = qSketchRegion(id + "F50", true);
            extrude(context, id + "F51", {"entities" : qUnion([Q0]), "depth" : 5 * mm});
        }
        {
            var Q0;
            Q0=makeQuery(id+"F51.opExtrude","CAP_FACE",FACE,{"disambiguationData":[OSD([sQuery(id+"F50.wireOp",EDGE,"E78.top"),sQuery(id+"F50.wireOp",EDGE,"E79.top"),sQuery(id+"F50.wireOp",EDGE,"E79.right"),sQuery(id+"F50.wireOp",EDGE,"E80.trimOffspring"),sQuery(id+"F50.wireOp",EDGE,"E81"),sQuery(id+"F50.wireOp",EDGE,"E82"),sQuery(id+"F50.wireOp",EDGE,"E83.trimOffspring"),sQuery(id+"F50.wireOp",EDGE,"E84"),sQuery(id+"F50.wireOp",EDGE,"E85"),sQuery(id+"F50.wireOp",EDGE,"E86"),sQuery(id+"F50.wireOp",EDGE,"E87"),sQuery(id+"F50.wireOp",EDGE,"E88.bottom"),sQuery(id+"F50.wireOp",EDGE,"E88.top"),sQuery(id+"F50.wireOp",EDGE,"E88.right")])],"isStart":false});
            var sketch = newSketch(context, id + "F52", { "sketchPlane" : qUnion([Q0])});
            skPoint(sketch, "E89.oppositeSnap0", {"position": v(-27.5, -1.9) * mm});
            skLineSegment(sketch, "E89.bottom", {"start": v(-34.31, 7.47) * mm, "end": v(-27.5, 7.47) * mm});
            skLineSegment(sketch, "E89.top", {"start": v(-34.31, -6.4) * mm, "end": v(-27.5, -6.4) * mm});
            skLineSegment(sketch, "E89.left", {"start": v(-34.31, 7.47) * mm, "end": v(-34.31, -6.4) * mm});
            skLineSegment(sketch, "E89.right", {"start": v(-27.5, 7.47) * mm, "end": v(-27.5, -6.4) * mm});
            skSolve(sketch);
        }
        {
            var Q0;
            Q0 = qSketchRegion(id + "F52", true);
            extrude(context, id + "F53", {"entities" : qUnion([Q0]), "operationType" : NewBodyOperationType.ADD, "depth" : 10 * mm});
        }
        {
            var Q0;
            Q0=makeQuery(id+"F46.imprint","IMPRINT",FACE,{"disambiguationData":[TD([[makeQuery(id+"F46.imprint","IMPRINT",EDGE,{"derivedFrom":makeQuery(id+"F10.opExtrude","CAP_EDGE",EDGE,{"disambiguationData":[OSD([sQuery(id+"F9.wireOp",EDGE,"E3.bottom")])],"isStart":false})}),1.0]])]});
            var sketch = newSketch(context, id + "F54", { "sketchPlane" : qUnion([Q0])});
            skSolve(sketch);
        }
        {
            var Q0;
            Q0=makeQuery(id+"F53.opExtrude","SWEPT_FACE",FACE,{"disambiguationData":[OSD([sQuery(id+"F52.wireOp",EDGE,"E89.left")])]});
            var sketch = newSketch(context, id + "F55", { "sketchPlane" : qUnion([Q0])});
            skLineSegment(sketch, "E90.bottom", {"start": v(-5.74, 42.52) * mm, "end": v(4.81, 42.52) * mm});
            skLineSegment(sketch, "E90.top", {"start": v(-5.74, 34) * mm, "end": v(4.81, 34) * mm});
            skLineSegment(sketch, "E90.left", {"start": v(-5.74, 42.52) * mm, "end": v(-5.74, 34) * mm});
            skLineSegment(sketch, "E90.right", {"start": v(4.81, 42.52) * mm, "end": v(4.81, 34) * mm});
            skSolve(sketch);
        }
        {
            var Q0;
            Q0 = qSketchRegion(id + "F55", true);
            extrude(context, id + "F56", {"entities" : qUnion([Q0]), "operationType" : NewBodyOperationType.REMOVE, "oppositeDirection" : true, "depth" : 6 * mm});
        }
        {
            var Q0;
            Q0=makeQuery(id+"F56.boolean.opBoolean","COPY",FACE,{"derivedFrom":makeQuery(id+"F56.opExtrude","CAP_FACE",FACE,{"disambiguationData":[OSD([sQuery(id+"F55.wireOp",EDGE,"E90.bottom"),sQuery(id+"F55.wireOp",EDGE,"E90.top"),sQuery(id+"F55.wireOp",EDGE,"E90.left"),sQuery(id+"F55.wireOp",EDGE,"E90.right")])],"isStart":false})});
            var sketch = newSketch(context, id + "F57", { "sketchPlane" : qUnion([Q0])});
            skCircle(sketch, "E91", {"center": v(0.55, 38.26) * mm, "radius": 4.26 * mm});
            skPoint(sketch, "E91.first.point", {"position": v(4.81, 38.48) * mm});
            skPoint(sketch, "E91.second.point", {"position": v(0.36, 34) * mm});
            skPoint(sketch, "E91.third.point", {"position": v(0.7, 42.52) * mm});
            skSolve(sketch);
        }
        {
            var Q0;
            Q0 = qSketchRegion(id + "F57", true);
            extrude(context, id + "F58", {"entities" : qUnion([Q0]), "operationType" : NewBodyOperationType.REMOVE, "oppositeDirection" : true, "depth" : 1 * mm});
        }
        {
            var Q0;
            Q0=makeQuery(id+"F54.imprint","IMPRINT",FACE,{"disambiguationData":[TD([[makeQuery(id+"F54.imprint","IMPRINT",EDGE,{"derivedFrom":makeQuery(id+"F46.imprint","IMPRINT",EDGE,{"derivedFrom":makeQuery(id+"F10.opExtrude","CAP_EDGE",EDGE,{"disambiguationData":[OSD([sQuery(id+"F9.wireOp",EDGE,"E3.bottom")])],"isStart":false})})}),1.0]])]});
            var sketch = newSketch(context, id + "F59", { "sketchPlane" : qUnion([Q0])});
            skLineSegment(sketch, "E92.bottom", {"start": v(-27.58, 11.69) * mm, "end": v(-53.43, 11.69) * mm});
            skLineSegment(sketch, "E92.top", {"start": v(-27.58, -11.57) * mm, "end": v(-53.43, -11.57) * mm});
            skLineSegment(sketch, "E92.left", {"start": v(-27.58, 11.69) * mm, "end": v(-27.58, -11.57) * mm});
            skLineSegment(sketch, "E92.right", {"start": v(-53.43, 11.69) * mm, "end": v(-53.43, -11.57) * mm});
            skSolve(sketch);
        }
        {
            var Q0;
            Q0=makeQuery(id+"F12.boolean.opBoolean","MERGE",FACE,{"derivedFrom":[makeQuery(id+"F10.opExtrude","SWEPT_FACE",FACE,{"disambiguationData":[OSD([sQuery(id+"F9.wireOp",EDGE,"E3.bottom")])]}),makeQuery(id+"F12.opExtrude","SWEPT_FACE",FACE,{"disambiguationData":[OSD([sQuery(id+"F11.wireOp",EDGE,"E4.bottom")])]})]});
            var sketch = newSketch(context, id + "F60", { "sketchPlane" : qUnion([Q0])});
            skLineSegment(sketch, "E93", {"start": v(-318.75, -72) * mm, "end": v(-347, -72) * mm});
            skLineSegment(sketch, "E94.top", {"start": v(-222.8, 15) * mm, "end": v(-209.26, 15) * mm});
            skPoint(sketch, "E95.end.orphan", {"position": v(-222.8, 26.16) * mm});
            skLineSegment(sketch, "E96", {"start": v(-347, -72) * mm, "end": v(-222.8, 26.16) * mm});
            skLineSegment(sketch, "E97", {"start": v(-332.87, -72) * mm, "end": v(-222.8, 15) * mm});
            skLineSegment(sketch, "E98", {"start": v(-209.26, 26.16) * mm, "end": v(-171.12, 15) * mm});
            skLineSegment(sketch, "E99", {"start": v(-171.12, 15) * mm, "end": v(-209.26, 15) * mm});
            skLineSegment(sketch, "E100", {"start": v(-222.8, 26.16) * mm, "end": v(-209.26, 26.16) * mm});
            skPoint(sketch, "E94.right.start.orphan", {"position": v(-209.26, 37.32) * mm});
            skPoint(sketch, "E101.end.orphan", {"position": v(-222.8, 37.32) * mm});
            skSolve(sketch);
        }
        {
            var Q0;
            Q0=makeQuery(id+"F60.imprint","IMPRINT",FACE,{"disambiguationData":[TD([[makeQuery(id+"F60.imprint","IMPRINT",EDGE,{"derivedFrom":sQuery(id+"F60.wireOp",EDGE,"E94.top")}),1.0]])]});
            extrude(context, id + "F61", {"entities" : qUnion([Q0]), "oppositeDirection" : true, "depth" : 160 * mm, "offsetDistance" : 25 * mm});
        }
    });
